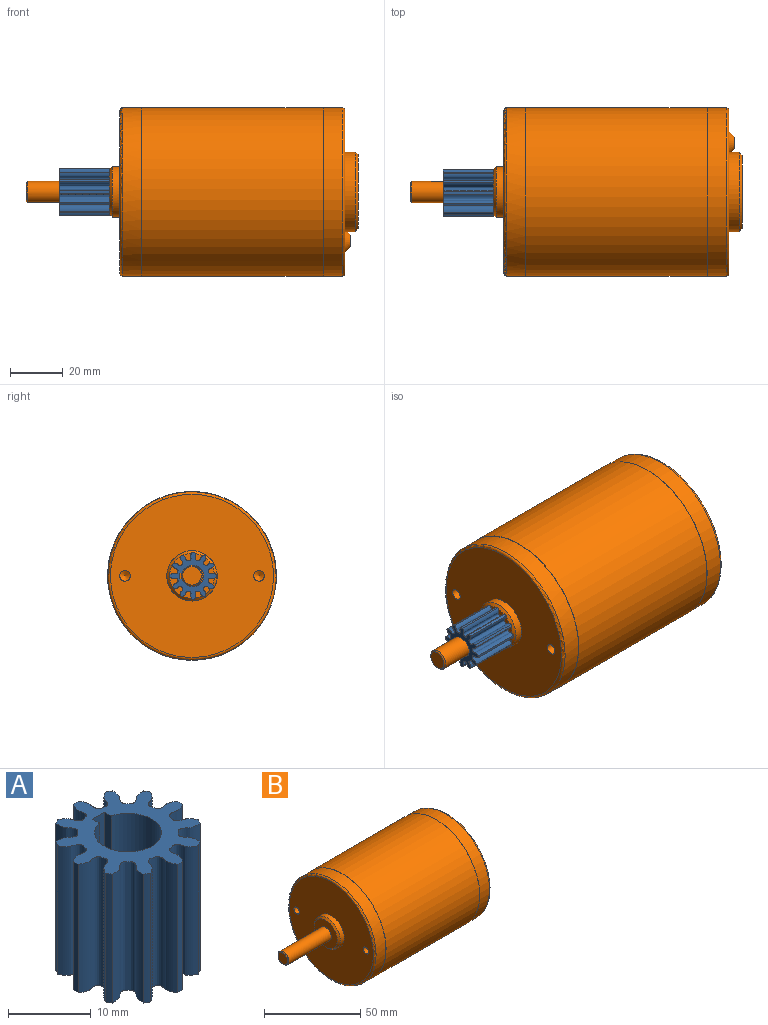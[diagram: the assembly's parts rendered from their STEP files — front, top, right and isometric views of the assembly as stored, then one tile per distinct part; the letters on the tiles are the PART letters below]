
ASSEMBLY  parts=2 mates=1
PART A: 30 faces, bbox 18x18x19.2 mm
  f0: cylinder r=4.03mm len=19mm, axis (0,0,-1), area 441.1mm2, adj f2,f26,f27,f28
  f1: cylinder r=8.89mm len=19mm, axis (0,0,1), area 17.2mm2, adj f2,f14,f15,f26
  f2: plane 17.95x17.95mm, normal (0,0,1), area 120.6mm2, adj f0,f1,f3,f4,f5,f6,f7,f8
  f3: cylinder r=8.89mm len=19mm, axis (0,0,1), area 17.2mm2, adj f2,f24,f25,f26
  f4: cylinder r=8.89mm len=19mm, axis (0,0,1), area 17.2mm2, adj f2,f14,f25,f26
  f5: cylinder r=8.89mm len=19mm, axis (0,0,1), area 17.2mm2, adj f2,f23,f24,f26
  f6: cylinder r=8.89mm len=19mm, axis (0,0,1), area 17.2mm2, adj f2,f22,f23,f26
  f7: cylinder r=8.89mm len=19mm, axis (0,0,1), area 17.2mm2, adj f2,f21,f22,f26
  f8: cylinder r=8.89mm len=19mm, axis (0,0,1), area 17.2mm2, adj f2,f20,f21,f26
  f9: cylinder r=8.89mm len=19mm, axis (0,0,1), area 17.2mm2, adj f2,f19,f20,f26
  f10: cylinder r=8.89mm len=19mm, axis (0,0,1), area 17.2mm2, adj f2,f18,f19,f26
  f11: cylinder r=8.89mm len=19mm, axis (0,0,1), area 17.2mm2, adj f2,f17,f18,f26
  f12: cylinder r=8.89mm len=19mm, axis (0,0,1), area 17.2mm2, adj f2,f16,f17,f26
  f13: cylinder r=8.89mm len=19mm, axis (0,0,1), area 17.2mm2, adj f2,f15,f16,f26
  f14: extruded ~19x3.59mm, area 135.8mm2, adj f1,f2,f4,f26
  f15: extruded ~19x3.59mm, area 135.8mm2, adj f1,f2,f13,f26
  f16: extruded ~19x3.56mm, area 135.8mm2, adj f2,f12,f13,f26
  f17: extruded ~19x3.59mm, area 135.8mm2, adj f2,f11,f12,f26
  f18: extruded ~19x3.59mm, area 135.8mm2, adj f2,f10,f11,f26
  f19: extruded ~19x3.56mm, area 135.8mm2, adj f2,f9,f10,f26
  f20: extruded ~19x3.59mm, area 135.8mm2, adj f2,f8,f9,f26
  f21: extruded ~19x3.59mm, area 135.8mm2, adj f2,f7,f8,f26
  f22: extruded ~19x3.56mm, area 135.8mm2, adj f2,f6,f7,f26
  f23: extruded ~19x3.59mm, area 135.8mm2, adj f2,f5,f6,f26
  f24: extruded ~19x3.59mm, area 135.8mm2, adj f2,f3,f5,f26
  f25: extruded ~19x3.56mm, area 135.8mm2, adj f2,f3,f4,f26
  f26: plane 17.95x17.95mm, normal (0,0,-1), area 118.5mm2, adj f0,f1,f3,f4,f5,f6,f7,f8
  f27: plane 19x1.13mm, normal (1,0,0), area 21.5mm2, adj f0,f2,f26,f29
  f28: plane 19x1.13mm, normal (-1,0,0), area 21.5mm2, adj f0,f2,f26,f29
  f29: plane 19x2.05mm, normal (0,-1,0), area 39mm2, adj f2,f26,f27,f28
PART B: 33 faces, bbox 125.8x69x69 mm
  f0: cone r=4mm half-angle=45deg, axis (1,0,0), area 16.7mm2, adj f18,f22
  f1: cone r=9.53mm half-angle=45deg, axis (1,0,0), area 81.4mm2, adj f13,f27
  f2: cone r=14.02mm half-angle=45deg, axis (-1,0,0), area 131.2mm2, adj f17,f23
  f3: cone r=2.12mm half-angle=45deg, axis (-1,0,0), area 62.9mm2, adj f5,f29
  f4: cone r=2.12mm half-angle=45deg, axis (-1,0,0), area 62.9mm2, adj f6,f28
  f5: cylinder r=4.32mm len=8.64mm, axis (-1,0,0), area 1.3mm2, adj f3,f21
  f6: cylinder r=4.32mm len=8.64mm, axis (-1,0,0), area 1.3mm2, adj f4,f21
  f7: cone r=2.02mm half-angle=59deg, axis (-1,0,0), area 14.9mm2, adj f8
  f8: cylinder r=2.02mm len=13.61mm, axis (-1,0,0), area 172.7mm2, adj f7,f26
  f9: cone r=2.02mm half-angle=59deg, axis (-1,0,0), area 14.9mm2, adj f10
  f10: cylinder r=2.02mm len=13.61mm, axis (-1,0,0), area 172.7mm2, adj f9,f26
  f11: torus R=30.88mm, axis (1,0,0), area 311mm2, adj f16,f21
  f12: torus R=30.88mm, axis (-1,0,0), area 311mm2, adj f14,f26
  f13: cylinder r=9.53mm len=19.05mm, axis (1,0,0), area 178.6mm2, adj f1,f26
  f14: cylinder r=31.88mm len=63.75mm, axis (1,0,0), area 1448mm2, adj f12,f25
  f15: cylinder r=32mm len=68.76mm, axis (1,0,0), area 13826.1mm2, adj f24,f25
  f16: cylinder r=31.88mm len=63.75mm, axis (1,0,0), area 1448mm2, adj f11,f24
  f17: cylinder r=15.04mm len=30.07mm, axis (1,0,0), area 376.4mm2, adj f2,f21
  f18: cylinder r=4mm len=31.1mm, axis (1,0,0), area 739mm2, adj f0,f19,f20,f27,f31,f32
  f19: cylinder r=1mm len=2mm, axis (0,1,0), area 3.4mm2, adj f18,f30,f31,f32
  f20: cylinder r=1mm len=2mm, axis (0,-1,0), area 3.4mm2, adj f18,f30,f31,f32
  f21: plane 61.75x61.75mm, normal (1,0,0), area 2167.7mm2, adj f5,f6,f11,f17
  f22: plane 7x7mm, normal (-1,0,0), area 38.5mm2, adj f0
  f23: plane 28.04x28.04mm, normal (1,0,0), area 617.6mm2, adj f2
  f24: plane 64.01x64.01mm, normal (1,0,0), area 25.5mm2, adj f15,f16
  f25: plane 64.01x64.01mm, normal (-1,0,0), area 25.5mm2, adj f14,f15
  f26: plane 61.75x61.75mm, normal (-1,0,0), area 2684.5mm2, adj f8,f10,f12,f13
  f27: plane 17.02x17.02mm, normal (-1,0,0), area 177.2mm2, adj f1,f18
  f28: plane 4.24x4.24mm, normal (1,0,0), area 14.1mm2, adj f4
  f29: plane 4.24x4.24mm, normal (1,0,0), area 14.1mm2, adj f3
  f30: plane 21.5x2mm, normal (0,1,0), area 42.1mm2, adj f19,f20,f31,f32
  f31: plane 19.5x1.07mm, normal (0,0,1), area 20.9mm2, adj f18,f19,f20,f30
  f32: plane 19.5x1.07mm, normal (0,0,-1), area 20.9mm2, adj f18,f19,f20,f30
PLACE A rot(axis=(0,1,0),90deg) t=(-50.45,-15.16,-13.73)mm
PLACE B t=(-36.95,-14.72,-13.73)mm
MATE fastened A.f2 <-> B.f0  axis (1,0,0) through (-40.95,-14.72,-13.73)mm
